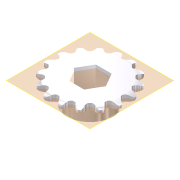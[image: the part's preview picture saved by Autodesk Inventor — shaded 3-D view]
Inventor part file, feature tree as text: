
AUTODESK INVENTOR PART (.ipt)
format: ipt  version: 2011 (Build 150239000, 239)  size: 497,152 bytes
history: native  units: mm
features: other x8, extrude x4, sketch x2, pattern_linear x1, pattern_circular x1
ambient origin geometry x8: Origin, YZ Plane, XZ Plane, XY Plane, X Axis, Y Axis, Z Axis, Center Point
bodies: Solid1 (feature_tree)
feature tree (16):
  other  "Blocks"
  other  "Theoretical Tooth Profile"
  other  "Tooth Profile"
  other  "Section Profile"
  other  "Shroud"
  other  "Strand"
  pattern_linear  "Strand Pattern"  Spacing1=1.6665mm  [1 undecoded]
  extrude  "Theoretical Tooth"  Depth=22.471114mm
  extrude  "Tooth"  Depth=2.530727mm
  pattern_circular  "Tooth Pattern"  [2 undecoded]
  other  "Timing Plane"
  extrude  "Extrusion4"  Depth=4.3065mm
  extrude  "Extrusion6"  Depth=4.62mm
  sketch  "Sketch4"  dims[d0=32.549026mm]
  other  "500Key"
  sketch  "Sketch6"  dims[d2=22.5deg d3=1.6665mm d10=22.471114mm d11=2.530727mm d12=2.64mm d13=4.3065mm d14=4.62mm d18=10.0mm d19=0.0mm d20=160.0mm d21=360.0deg d23=1.905mm d28=0.0mm d29=0.0mm d30=2.883mm d31=17.554806mm d32=2.883mm d33=0.8255mm d34=6.35mm d36=90.0deg d37=90.0deg d38=10.0mm d40=6.4mm d42=0.0mm d43=1.4415mm d44=23.452862mm d45=1.6665mm d46=7.128mm d47=0.0mm d48=25.4mm d49=0.0mm d50=10.0mm d51=21.59mm d52=7.493mm d53=0.0mm d54=12.7508mm d55=3.175mm d56=2.38125mm d59=12.7mm d60=25.4mm d61=0.0mm]
note: 3 required parameter values undecoded (feature->parameter linkage not recoverable at this tier; creation-order binding heuristic only, values carry confidence <= 0.55)
